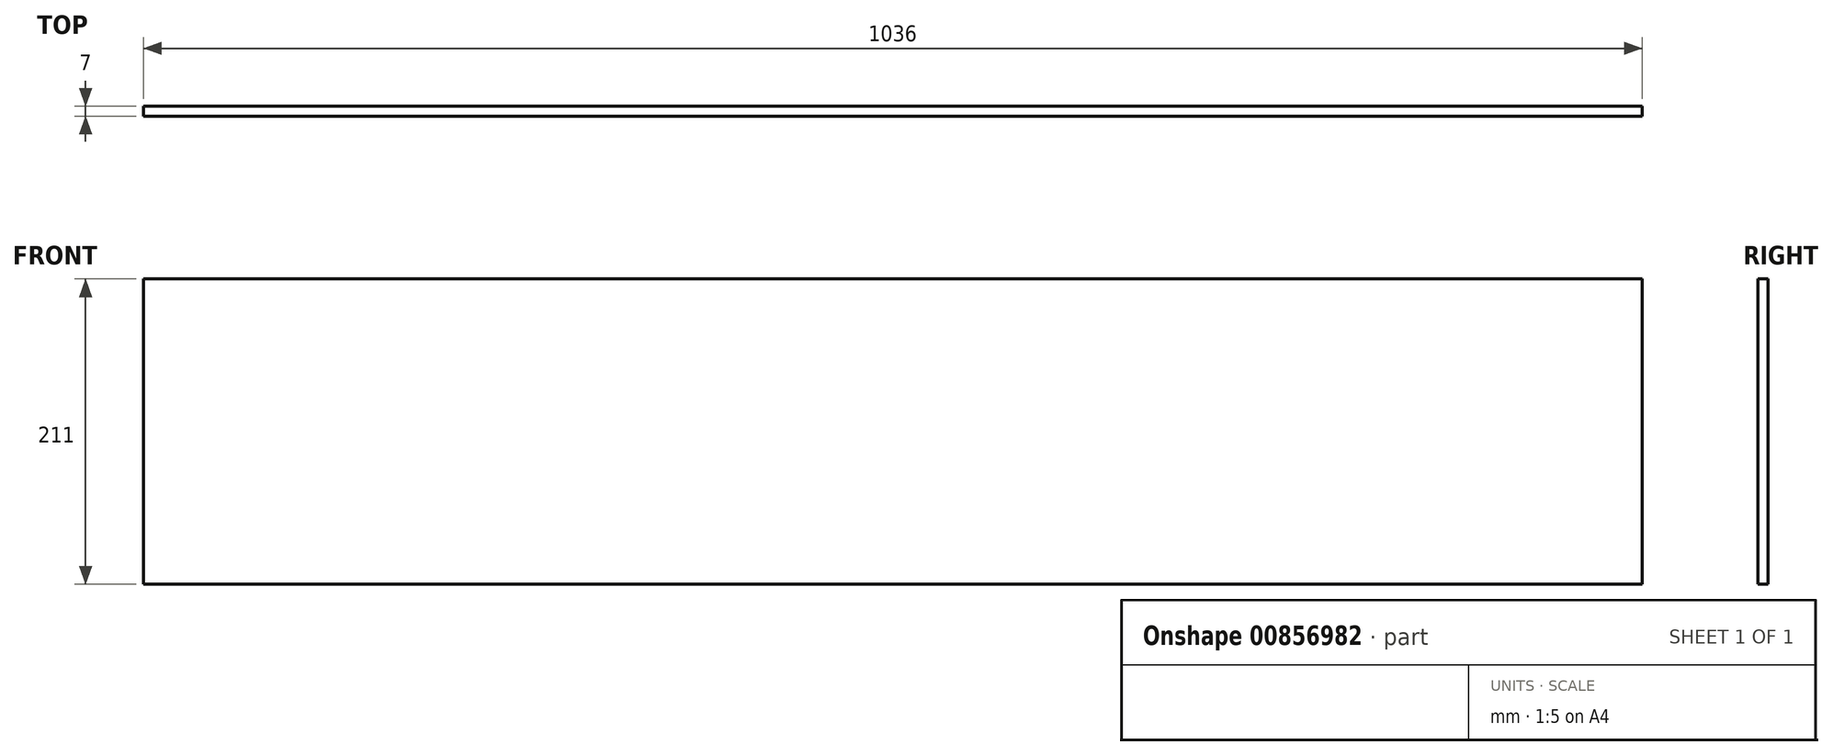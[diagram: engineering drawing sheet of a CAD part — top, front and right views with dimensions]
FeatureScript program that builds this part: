
annotation { "Feature Type Name" : "Feature", "Feature Type Description" : "" }
export const myFeature = defineFeature(function(context is Context, id is Id, definition is map)
    precondition{}
    {
        {
            var Q0;
            Q0=qCreatedBy(makeId("Front.planeOp"),FACE);
            var sketch = newSketch(context, id + "F0", { "sketchPlane" : qUnion([Q0])});
            skLineSegment(sketch, "E0.bottom", {"start": v(0, 0) * mm, "end": v(1036, 0) * mm});
            skLineSegment(sketch, "E0.top", {"start": v(0, -211) * mm, "end": v(1036, -211) * mm});
            skLineSegment(sketch, "E0.left", {"start": v(0, 0) * mm, "end": v(0, -211) * mm});
            skLineSegment(sketch, "E0.right", {"start": v(1036, 0) * mm, "end": v(1036, -211) * mm});
            skSolve(sketch);
        }
        {
            var Q0;
            Q0=makeQuery(id+"F0.imprint","IMPRINT",FACE,{"disambiguationData":[TD([[makeQuery(id+"F0.imprint","IMPRINT",EDGE,{"derivedFrom":sQuery(id+"F0.wireOp",EDGE,"E0.bottom")}),-1.0]])]});
            extrude(context, id + "F1", {"entities" : qUnion([Q0]), "oppositeDirection" : true, "depth" : 7 * mm, "offsetDistance" : 25 * mm});
        }
    });
